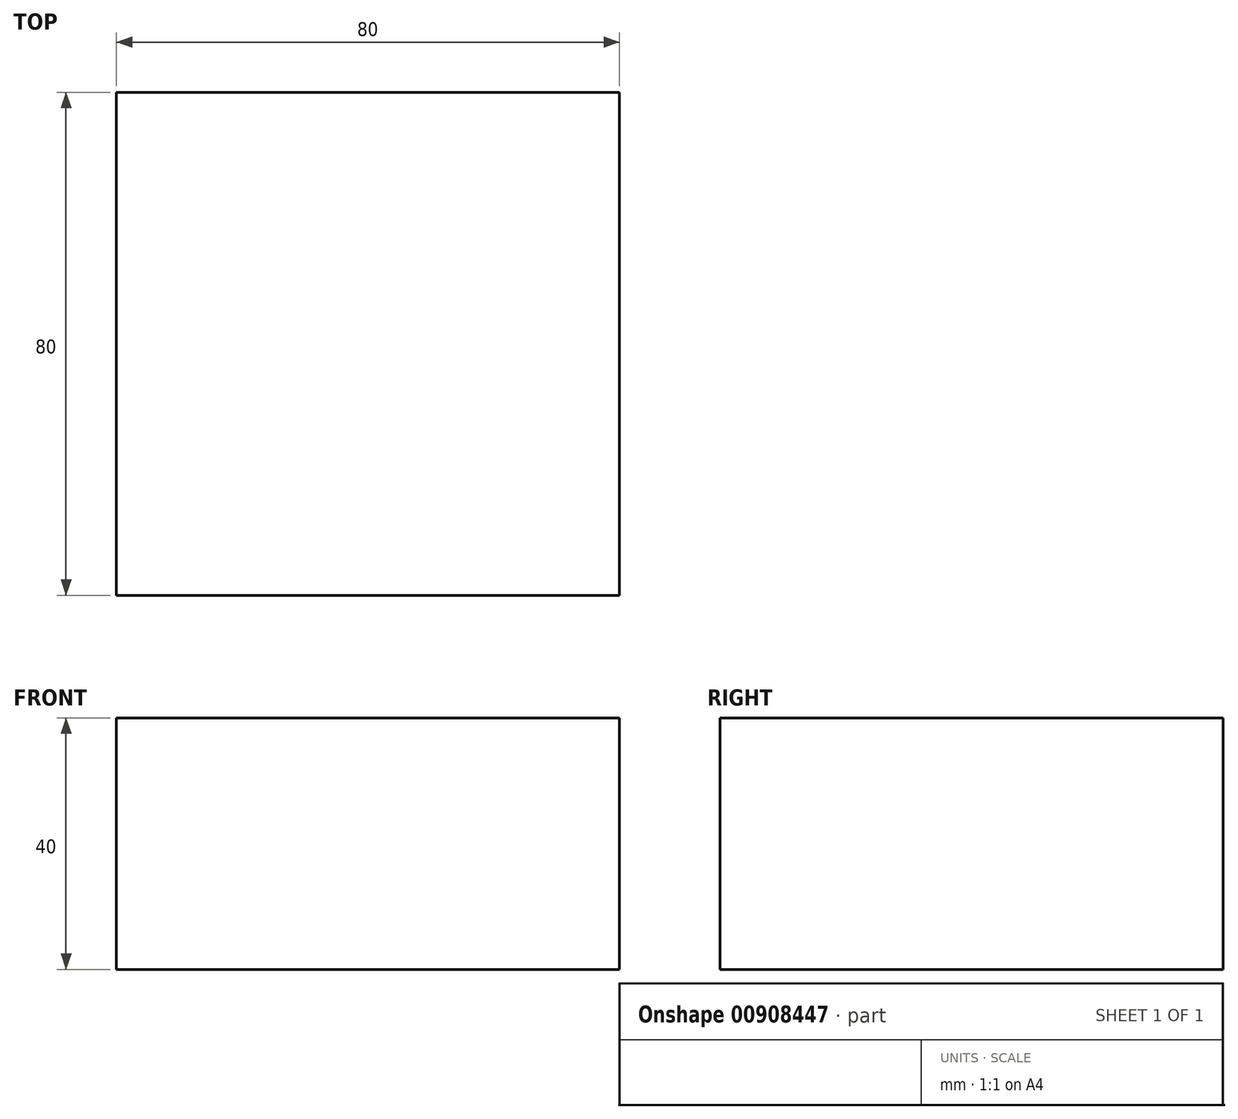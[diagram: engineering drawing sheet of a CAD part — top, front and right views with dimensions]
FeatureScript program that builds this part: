
annotation { "Feature Type Name" : "Feature", "Feature Type Description" : "" }
export const myFeature = defineFeature(function(context is Context, id is Id, definition is map)
    precondition{}
    {
        {
            var Q0;
            Q0=qCreatedBy(makeId("Top.planeOp"),FACE);
            var sketch = newSketch(context, id + "F0", { "sketchPlane" : qUnion([Q0])});
            skLineSegment(sketch, "E0.bottom", {"start": v(40, 40) * mm, "end": v(-40, 40) * mm});
            skLineSegment(sketch, "E0.top", {"start": v(40, -40) * mm, "end": v(-40, -40) * mm});
            skLineSegment(sketch, "E0.left", {"start": v(40, 40) * mm, "end": v(40, -40) * mm});
            skLineSegment(sketch, "E0.right", {"start": v(-40, 40) * mm, "end": v(-40, -40) * mm});
            skPoint(sketch, "E0.middle", {"position": v(0, 0) * mm});
            skSolve(sketch);
        }
        {
            var Q0;
            Q0=makeQuery(id+"F0.imprint","IMPRINT",FACE,{"disambiguationData":[TD([[makeQuery(id+"F0.imprint","IMPRINT",EDGE,{"derivedFrom":sQuery(id+"F0.wireOp",EDGE,"E0.bottom")}),1.0]])]});
            extrude(context, id + "F1", {"entities" : qUnion([Q0]), "depth" : 40 * mm, "offsetDistance" : 25 * mm});
        }
    });
